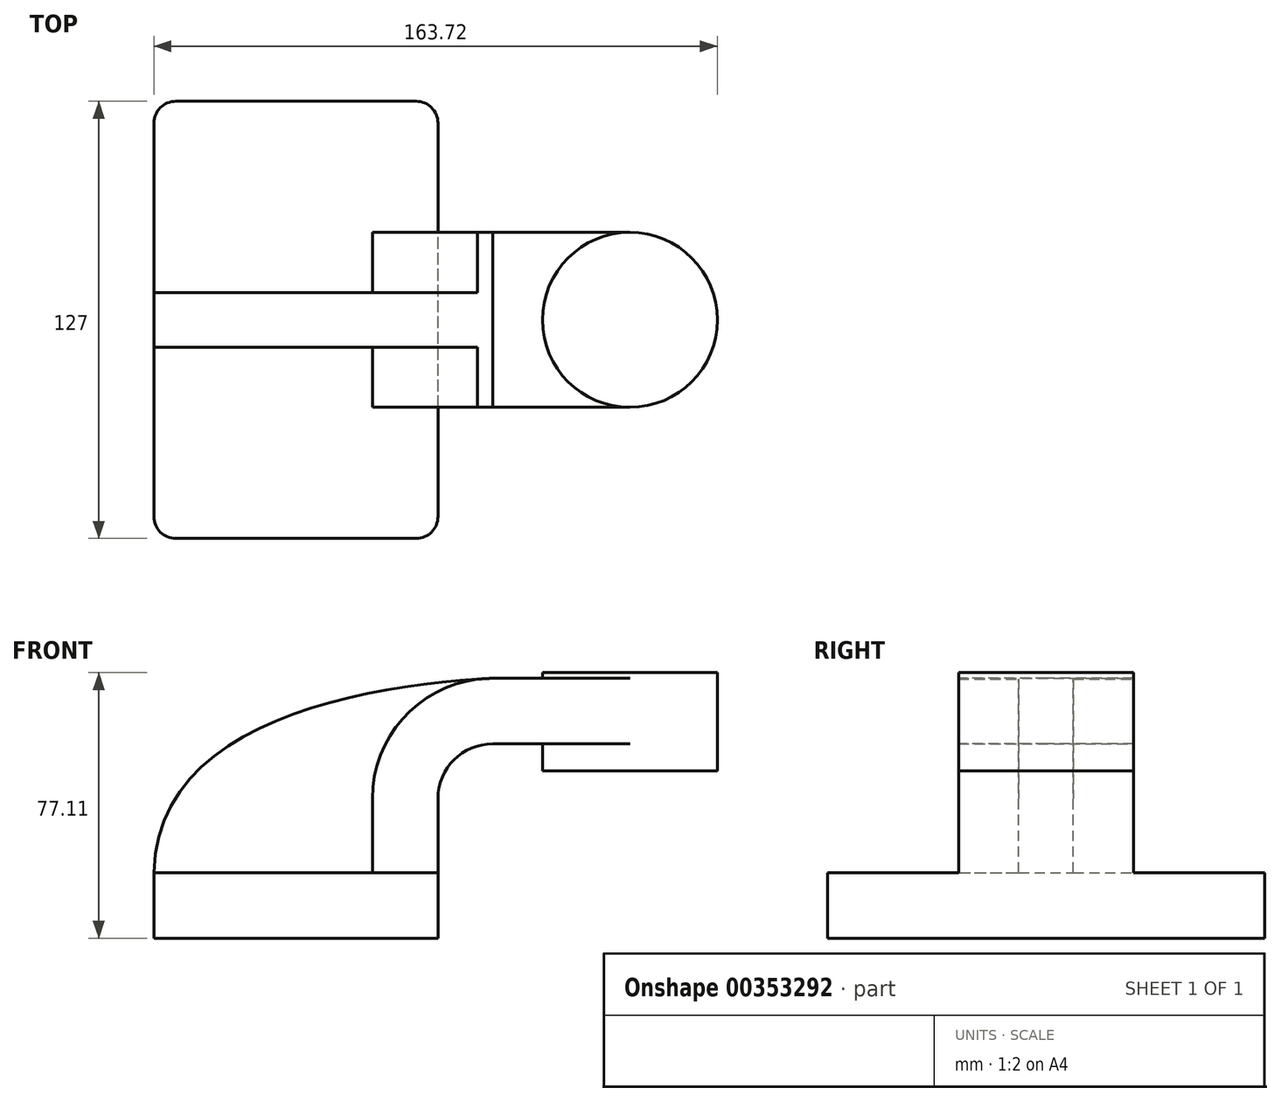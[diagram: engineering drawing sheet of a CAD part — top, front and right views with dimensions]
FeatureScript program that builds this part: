
annotation { "Feature Type Name" : "Feature", "Feature Type Description" : "" }
export const myFeature = defineFeature(function(context is Context, id is Id, definition is map)
    precondition{}
    {
        {
            var Q0;
            Q0=qCreatedBy(makeId("Front.planeOp"),FACE);
            var sketch = newSketch(context, id + "F0", { "sketchPlane" : qUnion([Q0])});
            skLineSegment(sketch, "E0.bottom", {"start": v(-41.28, 9.52) * mm, "end": v(41.27, 9.53) * mm});
            skLineSegment(sketch, "E0.top", {"start": v(-41.28, -9.53) * mm, "end": v(41.28, -9.53) * mm});
            skLineSegment(sketch, "E0.left", {"start": v(-41.28, 9.52) * mm, "end": v(-41.28, -9.53) * mm});
            skLineSegment(sketch, "E0.right", {"start": v(41.27, 9.53) * mm, "end": v(41.28, -9.52) * mm});
            skPoint(sketch, "E0.middle", {"position": v(0, 0) * mm});
            skLineSegment(sketch, "E1.bottom", {"start": v(71.64, 39) * mm, "end": v(122.44, 39) * mm});
            skLineSegment(sketch, "E1.top", {"start": v(71.64, 67.58) * mm, "end": v(122.44, 67.58) * mm});
            skLineSegment(sketch, "E1.left", {"start": v(71.64, 39) * mm, "end": v(71.64, 67.58) * mm});
            skLineSegment(sketch, "E1.right", {"start": v(122.44, 39) * mm, "end": v(122.44, 67.58) * mm});
            skPoint(sketch, "E1.middle", {"position": v(97.04, 53.29) * mm});
            skLineSegment(sketch, "E2", {"start": v(41.27, 9.53) * mm, "end": v(41.27, 31.06) * mm});
            skArc(sketch, "E3", {"start": v(41.28, 31.06) * mm, "mid": v(45.92, 42.28) * mm, "end": v(57.15, 46.93) * mm});
            skLineSegment(sketch, "E4", {"start": v(57.15, 46.93) * mm, "end": v(97.04, 46.93) * mm});
            skPoint(sketch, "E5", {"position": v(97.04, 39) * mm});
            skLineSegment(sketch, "E6.0", {"start": v(57.15, 65.98) * mm, "end": v(97.04, 65.98) * mm});
            skArc(sketch, "E6.1", {"start": v(22.23, 31.06) * mm, "mid": v(32.45, 55.75) * mm, "end": v(57.15, 65.98) * mm});
            skLineSegment(sketch, "E6.2", {"start": v(22.22, 9.53) * mm, "end": v(22.22, 31.06) * mm});
            skLineSegment(sketch, "E7", {"start": v(97.04, 39) * mm, "end": v(97.04, 67.58) * mm});
            skFitSpline(sketch, "E8", {"points": [v(-41.28, 9.52) * mm, v(57.15, 65.98) * mm], "startDerivative": vector(2.4, 132.1) * mm, "endDerivative": vector(114.47, 6.36) * mm});
            skSolve(sketch);
        }
        {
            var Q0;
            Q0=makeQuery(id+"F0.imprint","IMPRINT",FACE,{"disambiguationData":[TD([[makeQuery(id+"F0.imprint","IMPRINT",EDGE,{"derivedFrom":sQuery(id+"F0.wireOp",EDGE,"E0.top")}),1.0]])]});
            extrude(context, id + "F1", {"entities" : qUnion([Q0]), "endBound" : BoundingType.SYMMETRIC, "depth" : 127 * mm});
        }
        {
            var Q0;
            {var subQ1=sQuery(id+"F0.wireOp",EDGE,"E2");Q0=makeQuery(id+"F0.imprint","IMPRINT",FACE,{"disambiguationData":[TD([[makeQuery(id+"F0.imprint","IMPRINT",EDGE,{"derivedFrom":subQ1}),1.0]])]});}
            var Q1;
            {var subQ0=sQuery(id+"F0.wireOp",EDGE,"E4");var subQ1=sQuery(id+"F0.wireOp",EDGE,"E1.left");var subQ2=makeQuery(id+"F0.imprint","INTERSECT",VERTEX,{"derivedFrom":[subQ1,subQ0]});Q1=makeQuery(id+"F0.imprint","IMPRINT",FACE,{"disambiguationData":[TD([[makeQuery(id+"F0.imprint","IMPRINT",EDGE,{"disambiguationData":[TD([[subQ2,-1.0]])],"derivedFrom":subQ1}),-1.0]])]});}
            extrude(context, id + "F2", {"entities" : qUnion([Q0, Q1]), "operationType" : NewBodyOperationType.ADD, "endBound" : BoundingType.SYMMETRIC, "depth" : 50.8 * mm});
        }
        {
            var Q0;
            {var subQ3=sQuery(id+"F0.wireOp",EDGE,"E6.2");Q0=makeQuery(id+"F0.imprint","IMPRINT",FACE,{"disambiguationData":[TD([[makeQuery(id+"F0.imprint","IMPRINT",EDGE,{"derivedFrom":subQ3}),1.0]])]});}
            extrude(context, id + "F3", {"entities" : qUnion([Q0]), "operationType" : NewBodyOperationType.ADD, "endBound" : BoundingType.SYMMETRIC, "depth" : 15.88 * mm});
        }
        {
            var Q0;
            {var subQ4=sQuery(id+"F0.wireOp",EDGE,"E1.right");Q0=makeQuery(id+"F0.imprint","IMPRINT",FACE,{"disambiguationData":[TD([[makeQuery(id+"F0.imprint","IMPRINT",EDGE,{"derivedFrom":subQ4}),1.0]])]});}
            var Q1;
            Q1=sQuery(id+"F0.wireOp",EDGE,"E7");
            revolve(context, id + "F4", {"operationType" : NewBodyOperationType.ADD, "entities" : qUnion([Q0]), "axis" : qUnion([Q1]), "revolveType" : RevolveType.FULL});
        }
        {
            var Q0;
            Q0=makeQuery(id+"F1.opExtrude","CAP_EDGE",EDGE,{"disambiguationData":[OSD([sQuery(id+"F0.wireOp",EDGE,"E0.right")])],"isStart":false});
            var Q1;
            Q1=makeQuery(id+"F1.opExtrude","CAP_EDGE",EDGE,{"disambiguationData":[OSD([sQuery(id+"F0.wireOp",EDGE,"E0.left")])],"isStart":false});
            var Q2;
            Q2=makeQuery(id+"F1.opExtrude","CAP_EDGE",EDGE,{"disambiguationData":[OSD([sQuery(id+"F0.wireOp",EDGE,"E0.right")])],"isStart":true});
            var Q3;
            Q3=makeQuery(id+"F1.opExtrude","CAP_EDGE",EDGE,{"disambiguationData":[OSD([sQuery(id+"F0.wireOp",EDGE,"E0.left")])],"isStart":true});
            fillet(context, id + "F5", {"entities" : qUnion([Q0, Q1, Q2, Q3]), "radius" : 6.35 * mm, "tangentPropagation" : true, "allowEdgeOverflow" : false});
        }
    });
